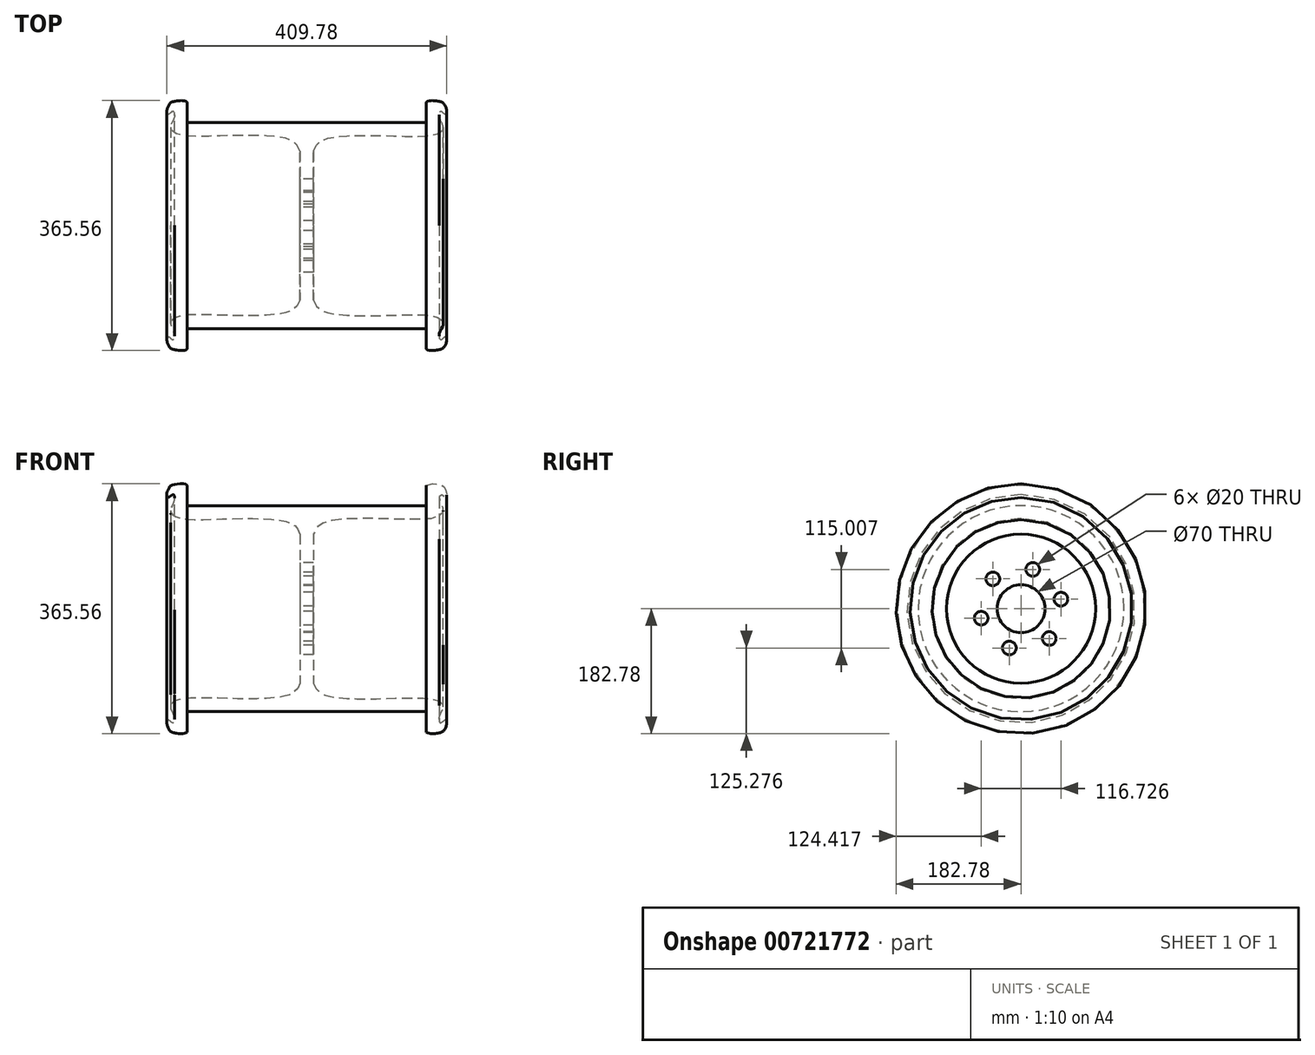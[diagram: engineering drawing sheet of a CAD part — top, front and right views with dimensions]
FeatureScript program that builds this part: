
annotation { "Feature Type Name" : "Feature", "Feature Type Description" : "" }
export const myFeature = defineFeature(function(context is Context, id is Id, definition is map)
    precondition{}
    {
        {
            var Q0;
            Q0=qCreatedBy(makeId("Front.planeOp"),FACE);
            var sketch = newSketch(context, id + "F0", { "sketchPlane" : qUnion([Q0])});
            skLineSegment(sketch, "E0", {"start": v(0, -109.4) * mm, "end": v(0, 298.81) * mm, "construction": true});
            skLineSegment(sketch, "E1", {"start": v(-273.05, 0) * mm, "end": v(346.86, 0) * mm, "construction": true});
            skLineSegment(sketch, "E2", {"start": v(0, 0) * mm, "end": v(-10, 0) * mm});
            skLineSegment(sketch, "E3", {"start": v(0, 150.68) * mm, "end": v(-175, 150.68) * mm});
            skLineSegment(sketch, "E4", {"start": v(-175, 150.68) * mm, "end": v(-175, 180.68) * mm});
            skFitSpline(sketch, "E5", {"points": [v(-175, 180.68) * mm, v(-197.38, 180.68) * mm, v(-201.21, 177.26) * mm, v(-204.8, 168.19) * mm, v(-203.01, 162.6) * mm, v(-196.05, 166.94) * mm, v(-193.7, 159.58) * mm, v(-199.49, 144.4) * mm, v(-191.98, 134.55) * mm, v(-121.03, 131.32) * mm, v(-27.88, 126.76) * mm, v(-10, 109.06) * mm], "startDerivative": vector(-118.03, 110.98) * mm, "endDerivative": vector(97.4, -283.35) * mm});
            skLineSegment(sketch, "E6", {"start": v(-10, 109.06) * mm, "end": v(-10, 0) * mm});
            skLineSegment(sketch, "E7.MirrorCS", {"start": v(0, 0) * mm, "end": v(10, 0) * mm});
            skFitSpline(sketch, "E8.MirrorCS", {"points": [v(175, 180.68) * mm, v(197.38, 180.68) * mm, v(201.21, 177.26) * mm, v(204.8, 168.19) * mm, v(203.01, 162.6) * mm, v(196.05, 166.94) * mm, v(193.7, 159.58) * mm, v(199.49, 144.4) * mm, v(191.98, 134.55) * mm, v(121.03, 131.32) * mm, v(27.88, 126.76) * mm, v(10, 109.06) * mm], "startDerivative": vector(118.03, 110.98) * mm, "endDerivative": vector(-97.4, -283.35) * mm});
            skLineSegment(sketch, "E9.MirrorCS", {"start": v(175, 150.68) * mm, "end": v(175, 180.68) * mm});
            skLineSegment(sketch, "E10.MirrorCS", {"start": v(10, 109.06) * mm, "end": v(10, 0) * mm});
            skLineSegment(sketch, "E11.MirrorCS", {"start": v(0, 150.68) * mm, "end": v(175, 150.68) * mm});
            skSolve(sketch);
        }
        {
            var Q0;
            Q0 = qSketchRegion(id + "F0", true);
            var Q1;
            Q1=sQuery(id+"F0.wireOp",EDGE,"E1");
            revolve(context, id + "F1", {"surfaceOperationType" : NewSurfaceOperationType.NEW, "entities" : qUnion([Q0]), "axis" : qUnion([Q1]), "revolveType" : RevolveType.FULL});
        }
        {
            var Q0;
            Q0=makeQuery(id+"F1.opRevolve","SWEPT_FACE",FACE,{"disambiguationData":[OSD([sQuery(id+"F0.wireOp",EDGE,"E6")])]});
            var sketch = newSketch(context, id + "F2", { "sketchPlane" : qUnion([Q0])});
            skCircle(sketch, "E12", {"center": v(0, 0) * mm, "radius": 35 * mm});
            skCircle(sketch, "E13", {"center": v(-17.13, 57.5) * mm, "radius": 10 * mm});
            skCircle(sketch, "E14.1.0", {"center": v(-58.36, 13.92) * mm, "radius": 10 * mm});
            skCircle(sketch, "E14.2.0", {"center": v(-41.24, -43.58) * mm, "radius": 10 * mm});
            skCircle(sketch, "E14.3.0", {"center": v(17.13, -57.5) * mm, "radius": 10 * mm});
            skCircle(sketch, "E14.4.0", {"center": v(58.36, -13.92) * mm, "radius": 10 * mm});
            skCircle(sketch, "E14.5.0", {"center": v(41.24, 43.58) * mm, "radius": 10 * mm});
            skSolve(sketch);
        }
        {
            var Q0;
            Q0=makeQuery(id+"F2.imprint","IMPRINT",FACE,{"disambiguationData":[TD([[makeQuery(id+"F2.imprint","IMPRINT",EDGE,{"derivedFrom":sQuery(id+"F2.wireOp",EDGE,"E13")}),1.0]])]});
            var Q1;
            Q1=makeQuery(id+"F2.imprint","IMPRINT",FACE,{"disambiguationData":[TD([[makeQuery(id+"F2.imprint","IMPRINT",EDGE,{"derivedFrom":sQuery(id+"F2.wireOp",EDGE,"E14.5.0")}),1.0]])]});
            var Q2;
            Q2=makeQuery(id+"F2.imprint","IMPRINT",FACE,{"disambiguationData":[TD([[makeQuery(id+"F2.imprint","IMPRINT",EDGE,{"derivedFrom":sQuery(id+"F2.wireOp",EDGE,"E14.4.0")}),1.0]])]});
            var Q3;
            Q3=makeQuery(id+"F2.imprint","IMPRINT",FACE,{"disambiguationData":[TD([[makeQuery(id+"F2.imprint","IMPRINT",EDGE,{"derivedFrom":sQuery(id+"F2.wireOp",EDGE,"E14.3.0")}),1.0]])]});
            var Q4;
            Q4=makeQuery(id+"F2.imprint","IMPRINT",FACE,{"disambiguationData":[TD([[makeQuery(id+"F2.imprint","IMPRINT",EDGE,{"derivedFrom":sQuery(id+"F2.wireOp",EDGE,"E14.2.0")}),1.0]])]});
            var Q5;
            Q5=makeQuery(id+"F2.imprint","IMPRINT",FACE,{"disambiguationData":[TD([[makeQuery(id+"F2.imprint","IMPRINT",EDGE,{"derivedFrom":sQuery(id+"F2.wireOp",EDGE,"E14.1.0")}),1.0]])]});
            var Q6;
            Q6=makeQuery(id+"F2.imprint","IMPRINT",FACE,{"disambiguationData":[TD([[makeQuery(id+"F2.imprint","IMPRINT",EDGE,{"derivedFrom":sQuery(id+"F2.wireOp",EDGE,"E12")}),1.0]])]});
            extrude(context, id + "F3", {"entities" : qUnion([Q0, Q1, Q2, Q3, Q4, Q5, Q6]), "operationType" : NewBodyOperationType.REMOVE, "endBound" : BoundingType.THROUGH_ALL, "oppositeDirection" : true, "depth" : 25 * mm, "offsetDistance" : 25 * mm});
        }
    });
